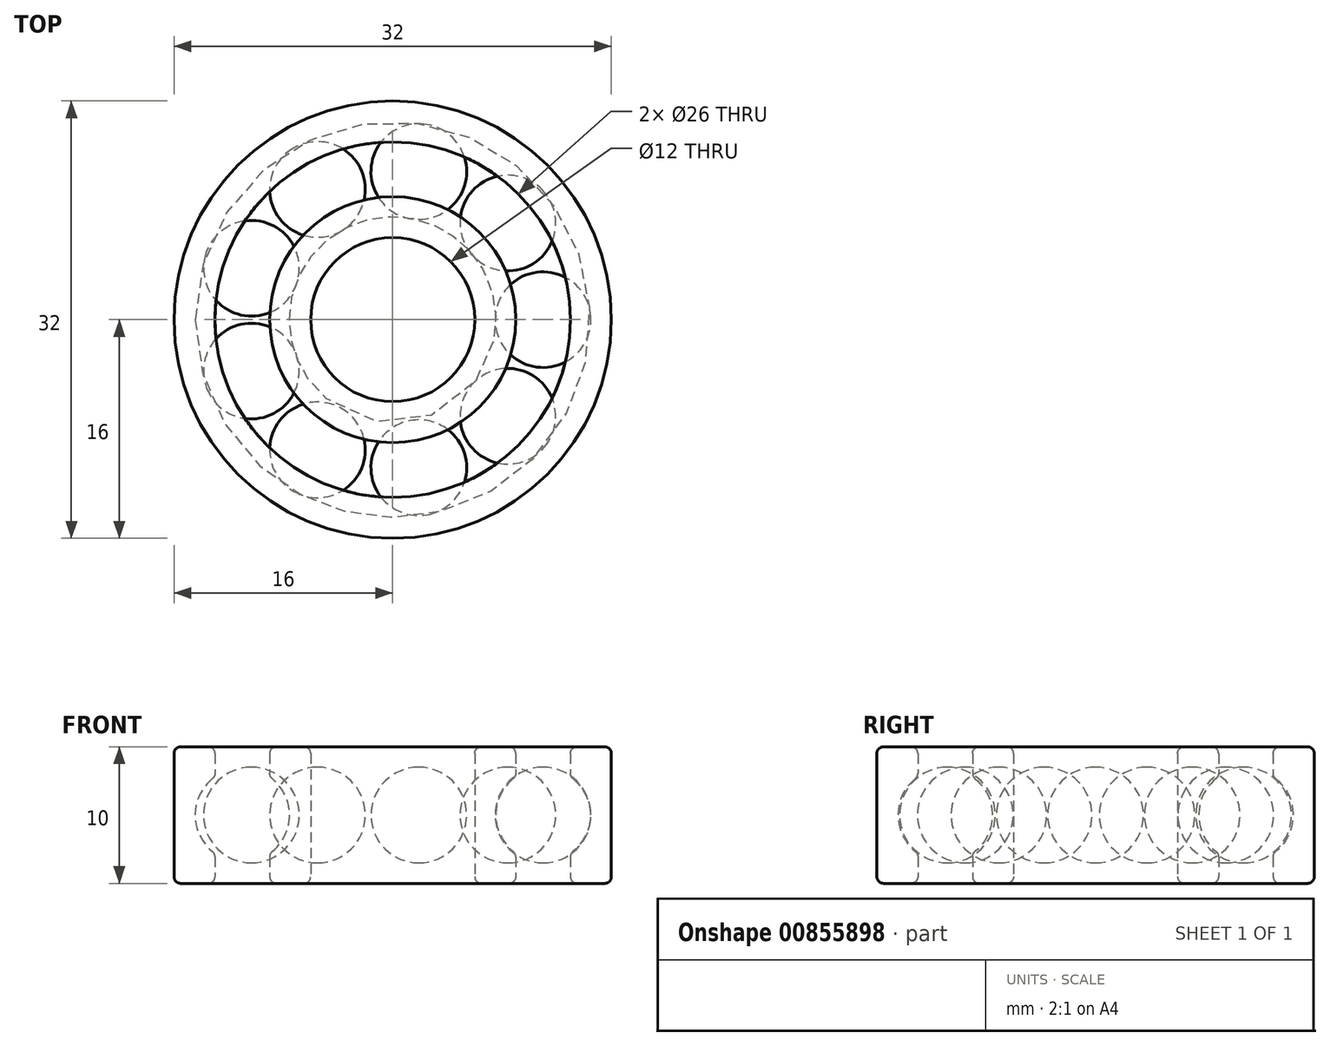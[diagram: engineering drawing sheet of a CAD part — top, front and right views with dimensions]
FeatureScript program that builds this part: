
annotation { "Feature Type Name" : "Feature", "Feature Type Description" : "" }
export const myFeature = defineFeature(function(context is Context, id is Id, definition is map)
    precondition{}
    {
        {
            var Q0;
            Q0=qCreatedBy(makeId("Front.planeOp"),FACE);
            var sketch = newSketch(context, id + "F0", { "sketchPlane" : qUnion([Q0])});
            skLineSegment(sketch, "E0.bottom", {"start": v(6, 5) * mm, "end": v(9, 5) * mm});
            skLineSegment(sketch, "E0.top", {"start": v(6, -5) * mm, "end": v(9, -5) * mm});
            skLineSegment(sketch, "E0.left", {"start": v(6, 5) * mm, "end": v(6, -5) * mm});
            skLineSegment(sketch, "E0.right", {"start": v(9, 5) * mm, "end": v(9, 2.81) * mm});
            skLineSegment(sketch, "E1.bottom", {"start": v(13, 5) * mm, "end": v(16, 5) * mm});
            skLineSegment(sketch, "E1.top", {"start": v(13, -5) * mm, "end": v(16, -5) * mm});
            skLineSegment(sketch, "E1.left", {"start": v(13, 5) * mm, "end": v(13, 2.81) * mm});
            skLineSegment(sketch, "E1.right", {"start": v(16, 5) * mm, "end": v(16, -5) * mm});
            skArc(sketch, "E2", {"start": v(9, 2.81) * mm, "mid": v(7.55, 0) * mm, "end": v(9, -2.81) * mm});
            skArc(sketch, "E3.trimOffspring", {"start": v(13, -2.81) * mm, "mid": v(14.45, 0) * mm, "end": v(13, 2.81) * mm});
            skLineSegment(sketch, "E4.trimOffspring", {"start": v(9, -2.81) * mm, "end": v(9, -5) * mm});
            skLineSegment(sketch, "E5.trimOffspring", {"start": v(13, -2.81) * mm, "end": v(13, -5) * mm});
            skSolve(sketch);
        }
        {
            var Q0;
            Q0=qCreatedBy(makeId("Right.planeOp"),FACE);
            var sketch = newSketch(context, id + "F1", { "sketchPlane" : qUnion([Q0])});
            skLineSegment(sketch, "E6", {"start": v(0, 0) * mm, "end": v(0, 39.58) * mm});
            skSolve(sketch);
        }
        {
            var Q0;
            Q0=qSketchRegion(id+"F0",true);
            var Q1;
            Q1=sQuery(id+"F1.wireOp",EDGE,"E6");
            revolve(context, id + "F2", {"surfaceOperationType" : NewSurfaceOperationType.NEW, "entities" : qUnion([Q0]), "axis" : qUnion([Q1]), "revolveType" : RevolveType.FULL});
        }
        {
            var Q0;
            Q0=qCreatedBy(makeId("Front.planeOp"),FACE);
            var sketch = newSketch(context, id + "F3", { "sketchPlane" : qUnion([Q0])});
            skArc(sketch, "E7", {"start": v(11, -3.5) * mm, "mid": v(14.5, 0) * mm, "end": v(11, 3.5) * mm});
            skLineSegment(sketch, "E8", {"start": v(11, 3.5) * mm, "end": v(11, -3.5) * mm});
            skSolve(sketch);
        }
        {
            var Q0;
            Q0=makeQuery(id+"F3.imprint","IMPRINT",FACE,{"disambiguationData":[TD([[makeQuery(id+"F3.imprint","IMPRINT",EDGE,{"derivedFrom":sQuery(id+"F3.wireOp",EDGE,"E7")}),1.0]])]});
            var Q1;
            Q1=sQuery(id+"F3.wireOp",EDGE,"E8");
            revolve(context, id + "F4", {"surfaceOperationType" : NewSurfaceOperationType.NEW, "entities" : qUnion([Q0]), "axis" : qUnion([Q1]), "revolveType" : RevolveType.FULL});
        }
        {
            var Q0;
            Q0=makeQuery(id+"F4.opRevolve","SWEPT_BODY",BODY,{"disambiguationData":[OSD([sQuery(id+"F3.wireOp",EDGE,"E7"),sQuery(id+"F3.wireOp",EDGE,"E8")])]});
            var Q1;
            Q1=sQuery(id+"F1.wireOp",EDGE,"E6");
            circularPattern(context, id + "F5", {"entities" : qUnion([Q0]), "axis" : qUnion([Q1]), "angle" : 360 * degree, "instanceCount" : 9, "equalSpace" : true});
        }
        {
            var Q0;
            Q0=makeQuery(id+"F2.opRevolve","SWEPT_FACE",FACE,{"disambiguationData":[OSD([sQuery(id+"F0.wireOp",EDGE,"E0.bottom")])]});
            var Q1;
            Q1=makeQuery(id+"F2.opRevolve","SWEPT_FACE",FACE,{"disambiguationData":[OSD([sQuery(id+"F0.wireOp",EDGE,"E1.bottom")])]});
            var Q2;
            Q2=makeQuery(id+"F2.opRevolve","SWEPT_FACE",FACE,{"disambiguationData":[OSD([sQuery(id+"F0.wireOp",EDGE,"E0.top")])]});
            var Q3;
            Q3=makeQuery(id+"F2.opRevolve","SWEPT_FACE",FACE,{"disambiguationData":[OSD([sQuery(id+"F0.wireOp",EDGE,"E1.top")])]});
            var Q4;
            Q4=makeQuery(id+"F2.opRevolve","SWEPT_EDGE",EDGE,{"disambiguationData":[OSD([sQuery(id+"F0.wireOp",EDGE,"E3.trimOffspring"),sQuery(id+"F0.wireOp",EDGE,"E5.trimOffspring")])]});
            var Q5;
            Q5=makeQuery(id+"F2.opRevolve","SWEPT_EDGE",EDGE,{"disambiguationData":[OSD([sQuery(id+"F0.wireOp",EDGE,"E2"),sQuery(id+"F0.wireOp",EDGE,"E4.trimOffspring")])]});
            var Q6;
            Q6=makeQuery(id+"F2.opRevolve","SWEPT_EDGE",EDGE,{"disambiguationData":[OSD([sQuery(id+"F0.wireOp",EDGE,"E1.left"),sQuery(id+"F0.wireOp",EDGE,"E3.trimOffspring")])]});
            var Q7;
            Q7=makeQuery(id+"F2.opRevolve","SWEPT_EDGE",EDGE,{"disambiguationData":[OSD([sQuery(id+"F0.wireOp",EDGE,"E0.right"),sQuery(id+"F0.wireOp",EDGE,"E2")])]});
            fillet(context, id + "F6", {"entities" : qUnion([Q0, Q1, Q2, Q3, Q4, Q5, Q6, Q7]), "radius" : .5 * mm, "tangentPropagation" : true, "allowEdgeOverflow" : false});
        }
    });
